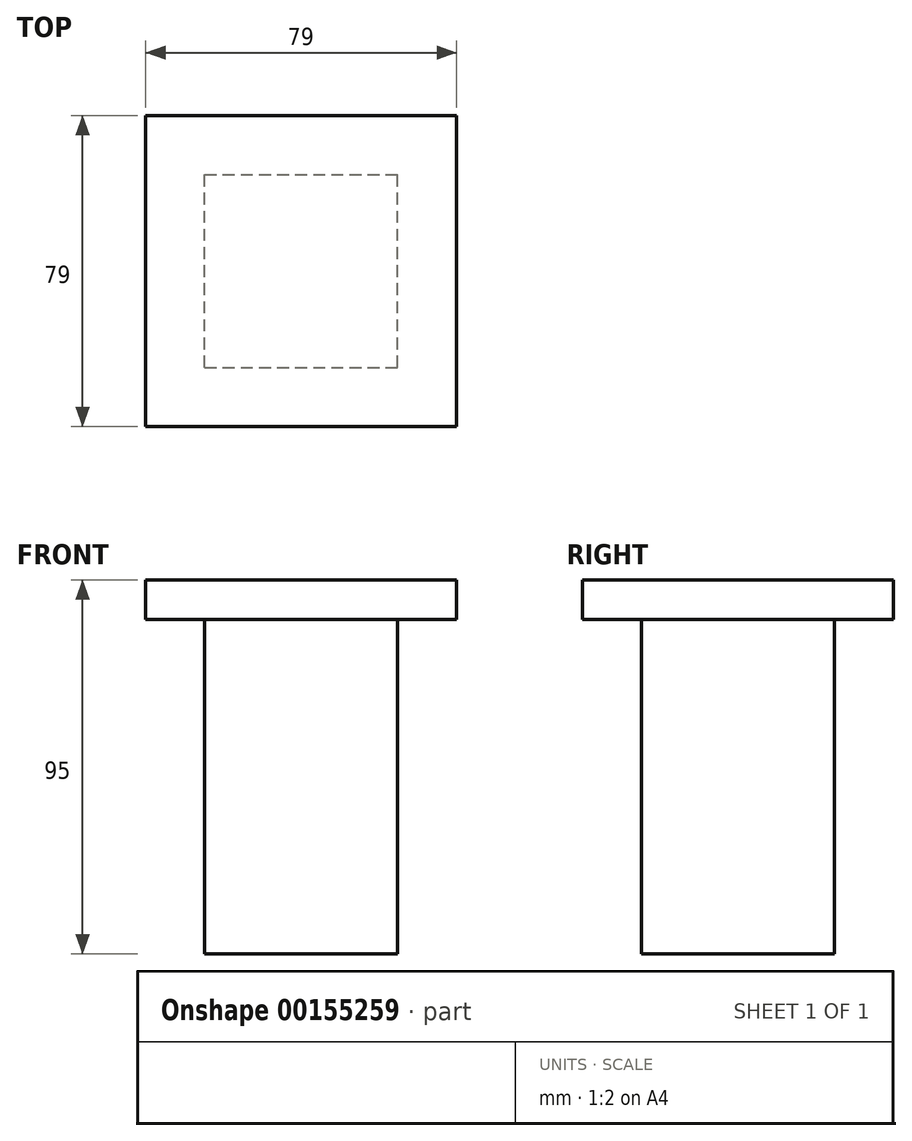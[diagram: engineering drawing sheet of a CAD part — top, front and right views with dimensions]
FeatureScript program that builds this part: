
annotation { "Feature Type Name" : "Feature", "Feature Type Description" : "" }
export const myFeature = defineFeature(function(context is Context, id is Id, definition is map)
    precondition{}
    {
        {
            var Q0;
            Q0=qCreatedBy(makeId("Top.planeOp"),FACE);
            var sketch = newSketch(context, id + "F0", { "sketchPlane" : qUnion([Q0])});
            skLineSegment(sketch, "E0.bottom", {"start": v(-39.5, -39.5) * mm, "end": v(39.5, -39.5) * mm});
            skLineSegment(sketch, "E0.top", {"start": v(-39.5, 39.5) * mm, "end": v(39.5, 39.5) * mm});
            skLineSegment(sketch, "E0.left", {"start": v(-39.5, -39.5) * mm, "end": v(-39.5, 39.5) * mm});
            skLineSegment(sketch, "E0.right", {"start": v(39.5, -39.5) * mm, "end": v(39.5, 39.5) * mm});
            skPoint(sketch, "E0.middle", {"position": v(0, 0) * mm});
            skSolve(sketch);
        }
        {
            var Q0;
            Q0=makeQuery(id+"F0.imprint","IMPRINT",FACE,{"disambiguationData":[TD([[makeQuery(id+"F0.imprint","IMPRINT",EDGE,{"derivedFrom":sQuery(id+"F0.wireOp",EDGE,"E0.bottom")}),1.0]])]});
            extrude(context, id + "F1", {"entities" : qUnion([Q0]), "depth" : 10 * mm});
        }
        {
            var Q0;
            Q0=makeQuery(id+"F1.opExtrude","CAP_FACE",FACE,{"disambiguationData":[OSD([sQuery(id+"F0.wireOp",EDGE,"E0.bottom"),sQuery(id+"F0.wireOp",EDGE,"E0.top"),sQuery(id+"F0.wireOp",EDGE,"E0.left"),sQuery(id+"F0.wireOp",EDGE,"E0.right")])],"isStart":false});
            var sketch = newSketch(context, id + "F2", { "sketchPlane" : qUnion([Q0])});
            skLineSegment(sketch, "E1.bottom", {"start": v(-24.5, -24.5) * mm, "end": v(24.5, -24.5) * mm});
            skLineSegment(sketch, "E1.top", {"start": v(-24.5, 24.5) * mm, "end": v(24.5, 24.5) * mm});
            skLineSegment(sketch, "E1.left", {"start": v(-24.5, -24.5) * mm, "end": v(-24.5, 24.5) * mm});
            skLineSegment(sketch, "E1.right", {"start": v(24.5, -24.5) * mm, "end": v(24.5, 24.5) * mm});
            skPoint(sketch, "E1.middle", {"position": v(0, 0) * mm});
            skSolve(sketch);
        }
        {
            var Q0;
            Q0 = qSketchRegion(id + "F2", true);
            extrude(context, id + "F3", {"entities" : qUnion([Q0]), "operationType" : NewBodyOperationType.ADD, "oppositeDirection" : true, "depth" : 95 * mm});
        }
    });
